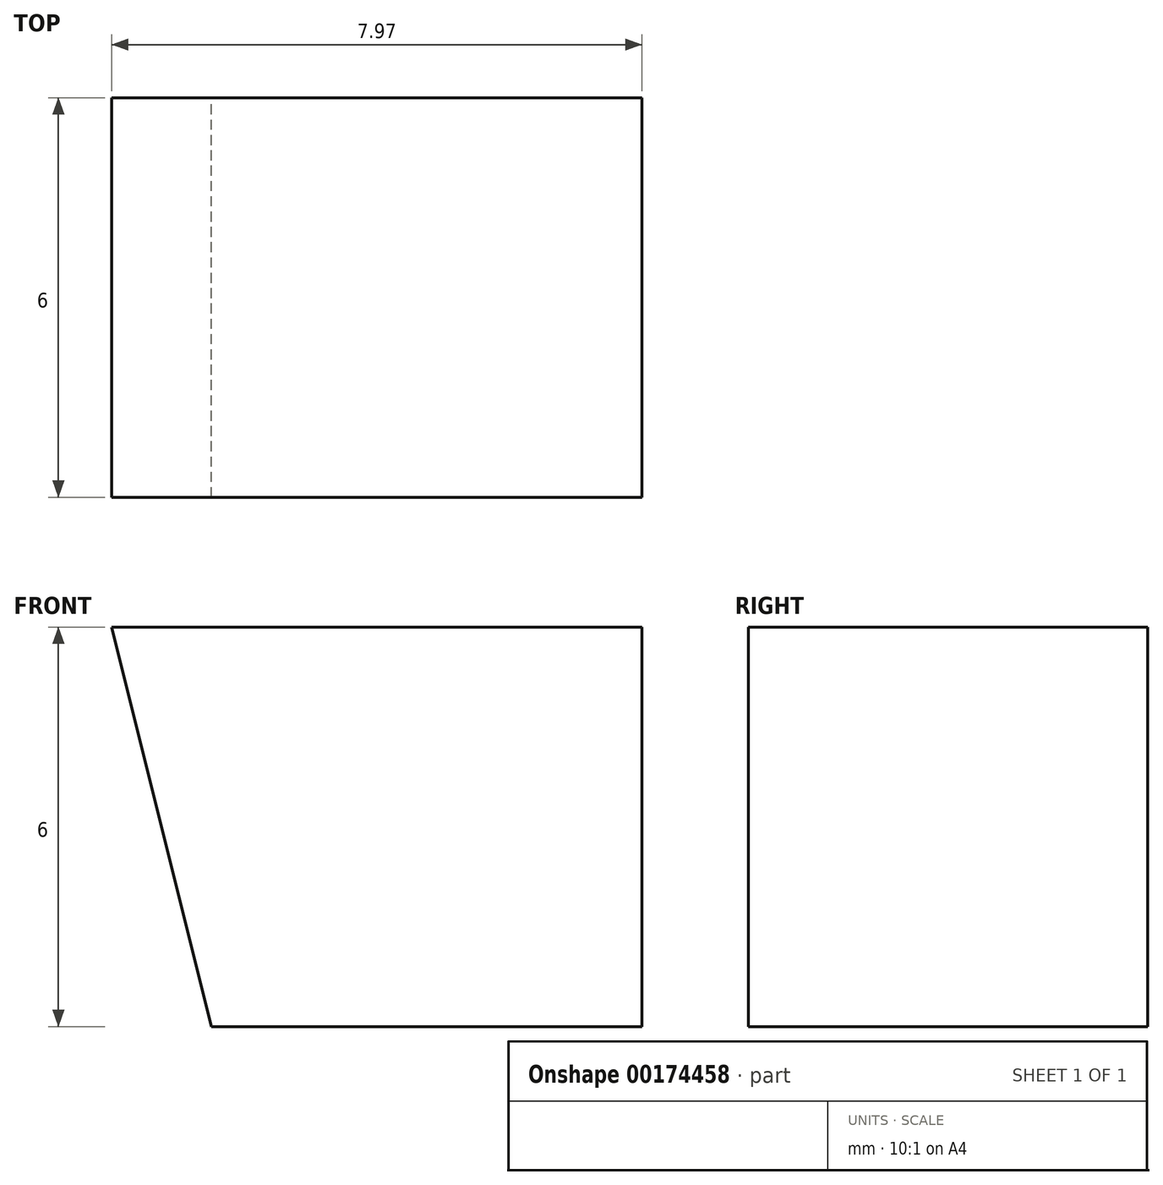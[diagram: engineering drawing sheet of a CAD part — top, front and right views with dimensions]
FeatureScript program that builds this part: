
annotation { "Feature Type Name" : "Feature", "Feature Type Description" : "" }
export const myFeature = defineFeature(function(context is Context, id is Id, definition is map)
    precondition{}
    {
        {
            var Q0;
            Q0=qCreatedBy(makeId("Front.planeOp"),FACE);
            var sketch = newSketch(context, id + "F0", { "sketchPlane" : qUnion([Q0])});
            skLineSegment(sketch, "E0.bottom", {"start": v(-100, 65) * mm, "end": v(100, 65) * mm});
            skLineSegment(sketch, "E0.top", {"start": v(-93.5, 0) * mm, "end": v(-83.5, 0) * mm});
            skLineSegment(sketch, "E0.left", {"start": v(-100, 65) * mm, "end": v(-100, 6) * mm});
            skLineSegment(sketch, "E0.right", {"start": v(100, 65) * mm, "end": v(100, 0) * mm});
            skLineSegment(sketch, "E1.0", {"start": v(-100, 6) * mm, "end": v(100, 6) * mm, "construction": true});
            skLineSegment(sketch, "E2", {"start": v(-92, 6) * mm, "end": v(-93.5, 0) * mm});
            skLineSegment(sketch, "E3", {"start": v(-85, 6) * mm, "end": v(-83.5, 0) * mm});
            skLineSegment(sketch, "E4.trimOffspring", {"start": v(-77, 0) * mm, "end": v(100, 0) * mm});
            skLineSegment(sketch, "E5", {"start": v(-83.5, 0) * mm, "end": v(-77, 0) * mm, "construction": true});
            skLineSegment(sketch, "E6", {"start": v(-100, 6) * mm, "end": v(-92, 6) * mm});
            skPoint(sketch, "E7.orphan", {"position": v(-100, 0) * mm});
            skLineSegment(sketch, "E8.1.0.0", {"start": v(-72.33, 6) * mm, "end": v(-73.83, 0) * mm});
            skLineSegment(sketch, "E8.1.0.1", {"start": v(-73.83, 0) * mm, "end": v(-63.83, 0) * mm});
            skLineSegment(sketch, "E8.1.0.2", {"start": v(-65.33, 6) * mm, "end": v(-63.83, 0) * mm});
            skLineSegment(sketch, "E8.2.0.0", {"start": v(-52.66, 6) * mm, "end": v(-54.16, 0) * mm});
            skLineSegment(sketch, "E8.2.0.1", {"start": v(-54.16, 0) * mm, "end": v(-44.16, 0) * mm});
            skLineSegment(sketch, "E8.2.0.2", {"start": v(-45.66, 6) * mm, "end": v(-44.16, 0) * mm});
            skLineSegment(sketch, "E8.3.0.0", {"start": v(-32.99, 6) * mm, "end": v(-34.49, 0) * mm});
            skLineSegment(sketch, "E8.3.0.1", {"start": v(-34.49, 0) * mm, "end": v(-24.5, 0) * mm});
            skLineSegment(sketch, "E8.3.0.2", {"start": v(-25.99, 6) * mm, "end": v(-24.5, 0) * mm});
            skLineSegment(sketch, "E8.4.0.0", {"start": v(-13.32, 6) * mm, "end": v(-14.82, 0) * mm});
            skLineSegment(sketch, "E8.4.0.1", {"start": v(-14.82, 0) * mm, "end": v(-4.82, 0) * mm});
            skLineSegment(sketch, "E8.4.0.2", {"start": v(-6.32, 6) * mm, "end": v(-4.82, 0) * mm});
            skLineSegment(sketch, "E8.5.0.0", {"start": v(6.35, 6) * mm, "end": v(4.85, 0) * mm});
            skLineSegment(sketch, "E8.5.0.1", {"start": v(4.85, 0) * mm, "end": v(14.85, 0) * mm});
            skLineSegment(sketch, "E8.5.0.2", {"start": v(13.35, 6) * mm, "end": v(14.85, 0) * mm});
            skLineSegment(sketch, "E8.6.0.0", {"start": v(26.02, 6) * mm, "end": v(24.52, 0) * mm});
            skLineSegment(sketch, "E8.6.0.1", {"start": v(24.52, 0) * mm, "end": v(34.52, 0) * mm});
            skLineSegment(sketch, "E8.6.0.2", {"start": v(33.02, 6) * mm, "end": v(34.52, 0) * mm});
            skLineSegment(sketch, "E8.7.0.0", {"start": v(45.7, 6) * mm, "end": v(44.2, 0) * mm});
            skLineSegment(sketch, "E8.7.0.1", {"start": v(44.2, 0) * mm, "end": v(54.19, 0) * mm});
            skLineSegment(sketch, "E8.7.0.2", {"start": v(52.7, 6) * mm, "end": v(54.19, 0) * mm});
            skLineSegment(sketch, "E8.8.0.0", {"start": v(65.36, 6) * mm, "end": v(63.86, 0) * mm});
            skLineSegment(sketch, "E8.8.0.1", {"start": v(63.86, 0) * mm, "end": v(73.86, 0) * mm});
            skLineSegment(sketch, "E8.8.0.2", {"start": v(72.36, 6) * mm, "end": v(73.86, 0) * mm});
            skLineSegment(sketch, "E8.9.0.0", {"start": v(85.03, 6) * mm, "end": v(83.53, 0) * mm});
            skLineSegment(sketch, "E8.9.0.1", {"start": v(83.53, 0) * mm, "end": v(93.53, 0) * mm});
            skLineSegment(sketch, "E8.9.0.2", {"start": v(92.03, 6) * mm, "end": v(93.53, 0) * mm});
            skLineSegment(sketch, "E8.direction1", {"start": v(-93.5, 0) * mm, "end": v(-73.83, 0) * mm, "construction": true});
            skPoint(sketch, "E9", {"position": v(92, 6) * mm});
            skLineSegment(sketch, "E10", {"start": v(92.03, 6) * mm, "end": v(100, 6) * mm});
            skSolve(sketch);
        }
        {
            var Q0;
            Q0 = qSketchRegion(id + "F0", true);
            extrude(context, id + "F1", {"entities" : qUnion([Q0]), "depth" : 6 * mm});
        }
    });
